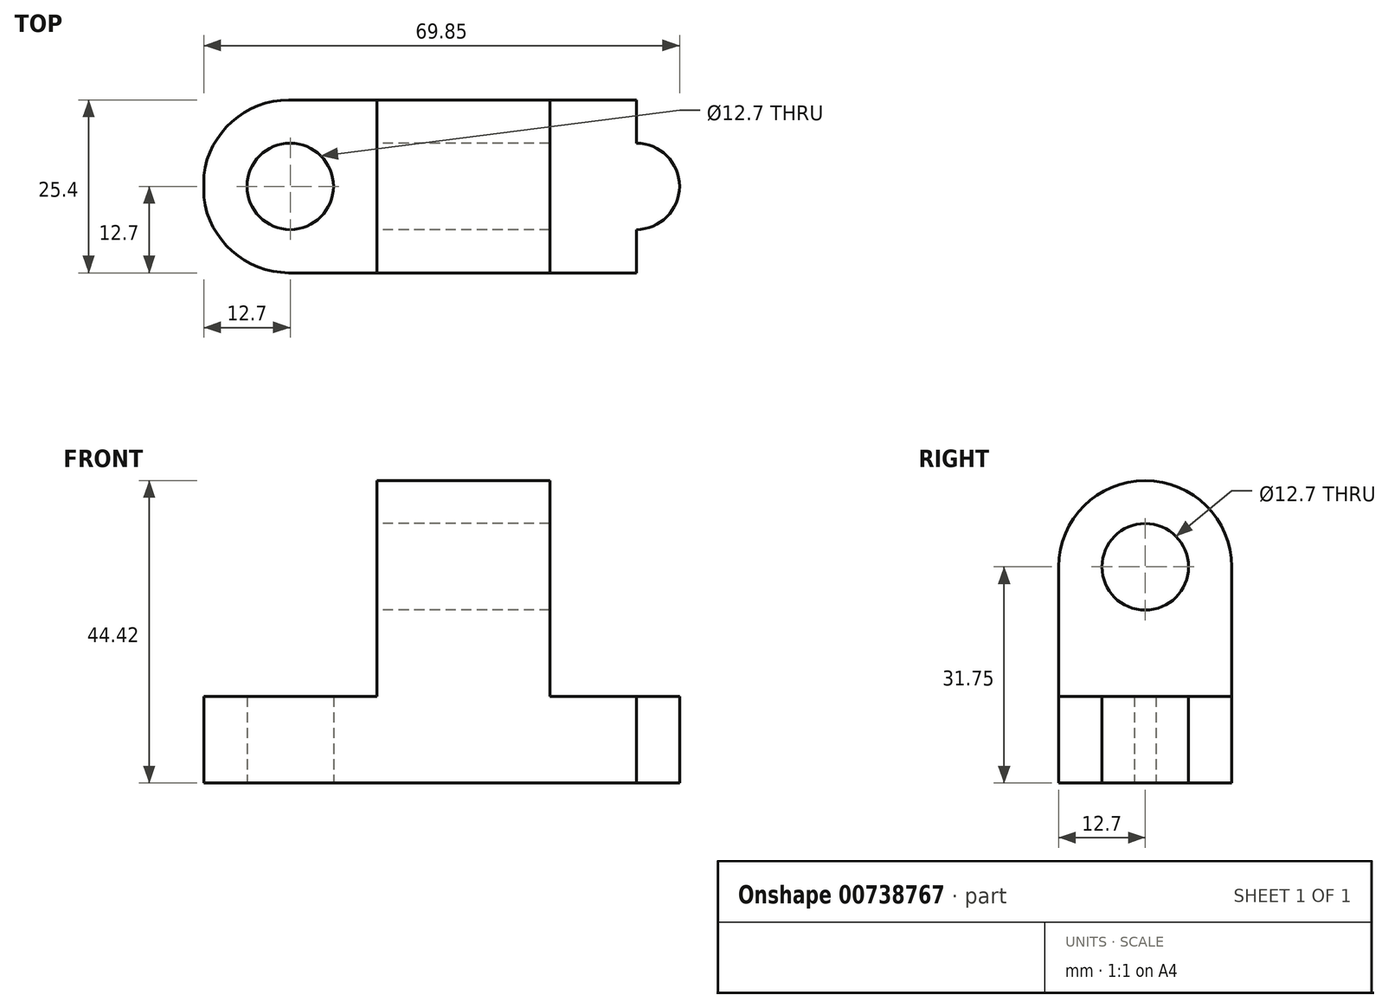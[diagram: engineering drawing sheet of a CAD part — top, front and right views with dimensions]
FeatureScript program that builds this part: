
annotation { "Feature Type Name" : "Feature", "Feature Type Description" : "" }
export const myFeature = defineFeature(function(context is Context, id is Id, definition is map)
    precondition{}
    {
        {
            var Q0;
            Q0=qCreatedBy(makeId("Front.planeOp"),FACE);
            var sketch = newSketch(context, id + "F0", { "sketchPlane" : qUnion([Q0])});
            skLineSegment(sketch, "E0", {"start": v(0, 0) * mm, "end": v(0, 12.7) * mm});
            skLineSegment(sketch, "E1", {"start": v(0, 12.7) * mm, "end": v(25.4, 12.7) * mm});
            skLineSegment(sketch, "E2", {"start": v(25.4, 12.7) * mm, "end": v(25.4, 44.45) * mm});
            skLineSegment(sketch, "E3", {"start": v(25.4, 44.45) * mm, "end": v(50.8, 44.45) * mm});
            skLineSegment(sketch, "E4", {"start": v(50.8, 44.45) * mm, "end": v(50.8, 12.7) * mm});
            skLineSegment(sketch, "E5", {"start": v(50.8, 12.7) * mm, "end": v(76.2, 12.7) * mm});
            skLineSegment(sketch, "E6", {"start": v(76.2, 12.7) * mm, "end": v(76.2, 0) * mm});
            skLineSegment(sketch, "E7", {"start": v(76.2, 0) * mm, "end": v(0, 0) * mm});
            skSolve(sketch);
        }
        {
            var Q0;
            Q0 = qSketchRegion(id + "F0", true);
            extrude(context, id + "F1", {"entities" : qUnion([Q0]), "depth" : 25.4 * mm, "offsetDistance" : 25.4 * mm});
        }
        {
            var Q0;
            Q0=qCreatedBy(makeId("Right.planeOp"),FACE);
            var sketch = newSketch(context, id + "F2", { "sketchPlane" : qUnion([Q0])});
            skLineSegment(sketch, "E8", {"start": v(-25.4, 31.75) * mm, "end": v(0, 31.75) * mm});
            skCircle(sketch, "E9", {"center": v(-12.7, 31.75) * mm, "radius": 6.35 * mm});
            skArc(sketch, "E10", {"start": v(0, 31.75) * mm, "mid": v(-12.7, 44.42) * mm, "end": v(-25.4, 31.75) * mm});
            skLineSegment(sketch, "E11", {"start": v(-25.4, 31.75) * mm, "end": v(-25.37, 44.47) * mm});
            skLineSegment(sketch, "E12", {"start": v(-25.37, 44.47) * mm, "end": v(0, 44.37) * mm});
            skLineSegment(sketch, "E13", {"start": v(0, 44.37) * mm, "end": v(0, 31.75) * mm});
            skLineSegment(sketch, "E14", {"start": v(-25.4, 31.75) * mm, "end": v(-25.4, 45.9) * mm});
            skLineSegment(sketch, "E15", {"start": v(-25.4, 45.9) * mm, "end": v(0, 45.8) * mm});
            skLineSegment(sketch, "E16", {"start": v(0, 45.8) * mm, "end": v(0, 31.75) * mm});
            skSolve(sketch);
        }
        {
            var Q0;
            {var subQ0=sQuery(id+"F2.wireOp",EDGE,"E9");var subQ1=sQuery(id+"F2.wireOp",EDGE,"E8");var subQ2=makeQuery(id+"F2.imprint","INTERSECT",VERTEX,{"disambiguationData":[OD(0.0)],"derivedFrom":[subQ1,subQ0]});Q0=makeQuery(id+"F2.imprint","IMPRINT",FACE,{"disambiguationData":[TD([[makeQuery(id+"F2.imprint","IMPRINT",EDGE,{"disambiguationData":[TD([[subQ2,-1.0]])],"derivedFrom":subQ1}),-1.0]])]});}
            var Q1;
            {var subQ0=sQuery(id+"F2.wireOp",EDGE,"E11");Q1=makeQuery(id+"F2.imprint","IMPRINT",FACE,{"disambiguationData":[TD([[makeQuery(id+"F2.imprint","IMPRINT",EDGE,{"derivedFrom":subQ0}),-1.0]])]});}
            var Q2;
            {var subQ0=sQuery(id+"F2.wireOp",EDGE,"E11");Q2=makeQuery(id+"F2.imprint","IMPRINT",FACE,{"disambiguationData":[TD([[makeQuery(id+"F2.imprint","IMPRINT",EDGE,{"derivedFrom":subQ0}),-1.0]])]});}
            var Q3;
            {var subQ0=sQuery(id+"F2.wireOp",EDGE,"E9");var subQ1=sQuery(id+"F2.wireOp",EDGE,"E8");var subQ2=makeQuery(id+"F2.imprint","INTERSECT",VERTEX,{"disambiguationData":[OD(0.0)],"derivedFrom":[subQ1,subQ0]});Q3=makeQuery(id+"F2.imprint","IMPRINT",FACE,{"disambiguationData":[TD([[makeQuery(id+"F2.imprint","IMPRINT",EDGE,{"disambiguationData":[TD([[subQ2,-1.0]])],"derivedFrom":subQ1}),1.0]])]});}
            var Q4;
            {var subQ0=sQuery(id+"F2.wireOp",EDGE,"E13");Q4=makeQuery(id+"F2.imprint","IMPRINT",FACE,{"disambiguationData":[TD([[makeQuery(id+"F2.imprint","IMPRINT",EDGE,{"derivedFrom":subQ0}),-1.0]])]});}
            var Q5;
            {var subQ3=sQuery(id+"F2.wireOp",EDGE,"E11");Q5=makeQuery(id+"F2.imprint","IMPRINT",FACE,{"disambiguationData":[TD([[makeQuery(id+"F2.imprint","IMPRINT",EDGE,{"derivedFrom":subQ3}),1.0]])]});}
            extrude(context, id + "F3", {"entities" : qUnion([Q0, Q1, Q2, Q3, Q4, Q5]), "operationType" : NewBodyOperationType.REMOVE, "endBound" : BoundingType.THROUGH_ALL, "depth" : 25.4 * mm, "offsetDistance" : 25.4 * mm});
        }
        {
            var Q0;
            Q0=qCreatedBy(makeId("Top.planeOp"),FACE);
            var sketch = newSketch(context, id + "F4", { "sketchPlane" : qUnion([Q0])});
            skLineSegment(sketch, "E17", {"start": v(12.7, 0) * mm, "end": v(12.7, -25.4) * mm});
            skCircle(sketch, "E18", {"center": v(12.7, -12.7) * mm, "radius": 6.35 * mm});
            skArc(sketch, "E19", {"start": v(12.7, 0) * mm, "mid": v(-0.1, -12.7) * mm, "end": v(12.7, -25.4) * mm});
            skLineSegment(sketch, "E20", {"start": v(12.7, -25.4) * mm, "end": v(-2.28, -25.52) * mm});
            skLineSegment(sketch, "E21", {"start": v(-2.28, -25.52) * mm, "end": v(-2.48, 0) * mm});
            skLineSegment(sketch, "E22", {"start": v(-2.48, 0) * mm, "end": v(12.7, 0) * mm});
            skSolve(sketch);
        }
        {
            var Q0;
            {var subQ0=sQuery(id+"F4.wireOp",EDGE,"E18");var subQ1=sQuery(id+"F4.wireOp",EDGE,"E17");var subQ2=makeQuery(id+"F4.imprint","INTERSECT",VERTEX,{"disambiguationData":[OD(0.0)],"derivedFrom":[subQ1,subQ0]});Q0=makeQuery(id+"F4.imprint","IMPRINT",FACE,{"disambiguationData":[TD([[makeQuery(id+"F4.imprint","IMPRINT",EDGE,{"disambiguationData":[TD([[subQ2,-1.0]])],"derivedFrom":subQ1}),1.0]])]});}
            var Q1;
            {var subQ0=sQuery(id+"F4.wireOp",EDGE,"E19");Q1=makeQuery(id+"F4.imprint","IMPRINT",FACE,{"disambiguationData":[TD([[makeQuery(id+"F4.imprint","IMPRINT",EDGE,{"derivedFrom":subQ0}),-1.0]])]});}
            var Q2;
            {var subQ0=sQuery(id+"F4.wireOp",EDGE,"E18");var subQ1=sQuery(id+"F4.wireOp",EDGE,"E17");var subQ2=makeQuery(id+"F4.imprint","INTERSECT",VERTEX,{"disambiguationData":[OD(0.0)],"derivedFrom":[subQ1,subQ0]});Q2=makeQuery(id+"F4.imprint","IMPRINT",FACE,{"disambiguationData":[TD([[makeQuery(id+"F4.imprint","IMPRINT",EDGE,{"disambiguationData":[TD([[subQ2,-1.0]])],"derivedFrom":subQ1}),-1.0]])]});}
            var Q3;
            Q3=makeQuery(id+"F1.opExtrude","SWEPT_FACE",FACE,{"disambiguationData":[OSD([sQuery(id+"F0.wireOp",EDGE,"E1")])]});
            extrude(context, id + "F5", {"entities" : qUnion([Q0, Q1, Q2, Q3]), "operationType" : NewBodyOperationType.REMOVE, "endBound" : BoundingType.THROUGH_ALL, "depth" : 25.4 * mm, "offsetDistance" : 25.4 * mm});
        }
        {
            var Q0;
            Q0=qCreatedBy(makeId("Top.planeOp"),FACE);
            var sketch = newSketch(context, id + "F6", { "sketchPlane" : qUnion([Q0])});
            skLineSegment(sketch, "E23", {"start": v(63.5, 0) * mm, "end": v(63.5, -25.4) * mm});
            skCircle(sketch, "E24", {"center": v(63.5, -12.7) * mm, "radius": 6.35 * mm});
            skArc(sketch, "E25", {"start": v(63.5, -25.4) * mm, "mid": v(76.24, -12.7) * mm, "end": v(63.5, 0) * mm});
            skLineSegment(sketch, "E26", {"start": v(63.5, 0) * mm, "end": v(77.44, 0.05) * mm});
            skLineSegment(sketch, "E27", {"start": v(77.44, 0.05) * mm, "end": v(77.52, -25.42) * mm});
            skLineSegment(sketch, "E28", {"start": v(77.52, -25.42) * mm, "end": v(63.5, -25.4) * mm});
            skSolve(sketch);
        }
        {
            var Q0;
            {var subQ0=sQuery(id+"F6.wireOp",EDGE,"E24");var subQ1=sQuery(id+"F6.wireOp",EDGE,"E23");var subQ2=makeQuery(id+"F6.imprint","INTERSECT",VERTEX,{"disambiguationData":[OD(0.0)],"derivedFrom":[subQ1,subQ0]});Q0=makeQuery(id+"F6.imprint","IMPRINT",FACE,{"disambiguationData":[TD([[makeQuery(id+"F6.imprint","IMPRINT",EDGE,{"disambiguationData":[TD([[subQ2,-1.0]])],"derivedFrom":subQ1}),-1.0]])]});}
            var Q1;
            {var subQ0=sQuery(id+"F6.wireOp",EDGE,"E25");Q1=makeQuery(id+"F6.imprint","IMPRINT",FACE,{"disambiguationData":[TD([[makeQuery(id+"F6.imprint","IMPRINT",EDGE,{"derivedFrom":subQ0}),-1.0]])]});}
            var Q2;
            {var subQ0=sQuery(id+"F6.wireOp",EDGE,"E24");var subQ1=sQuery(id+"F6.wireOp",EDGE,"E23");var subQ2=makeQuery(id+"F6.imprint","INTERSECT",VERTEX,{"disambiguationData":[OD(0.0)],"derivedFrom":[subQ1,subQ0]});Q2=makeQuery(id+"F6.imprint","IMPRINT",FACE,{"disambiguationData":[TD([[makeQuery(id+"F6.imprint","IMPRINT",EDGE,{"disambiguationData":[TD([[subQ2,-1.0]])],"derivedFrom":subQ1}),1.0]])]});}
            extrude(context, id + "F7", {"entities" : qUnion([Q0, Q1, Q2]), "operationType" : NewBodyOperationType.REMOVE, "endBound" : BoundingType.THROUGH_ALL, "depth" : 25.4 * mm, "offsetDistance" : 25.4 * mm});
        }
    });
